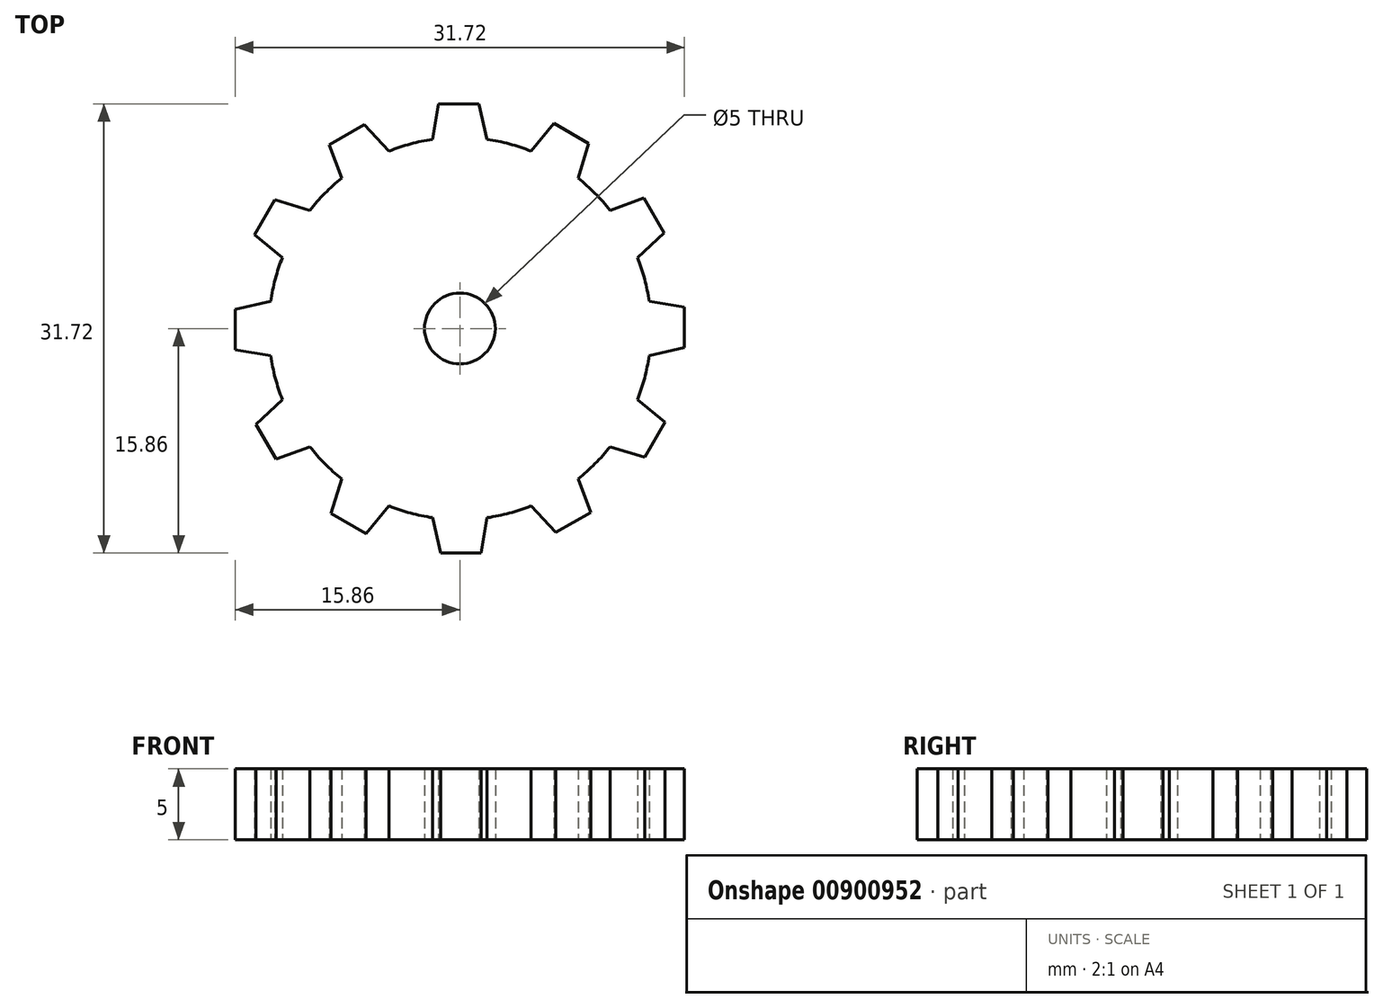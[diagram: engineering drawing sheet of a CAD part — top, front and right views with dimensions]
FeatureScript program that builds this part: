
annotation { "Feature Type Name" : "Feature", "Feature Type Description" : "" }
export const myFeature = defineFeature(function(context is Context, id is Id, definition is map)
    precondition{}
    {
        {
            var Q0;
            Q0=qCreatedBy(makeId("Top.planeOp"),FACE);
            var sketch = newSketch(context, id + "F0", { "sketchPlane" : qUnion([Q0])});
            skCircle(sketch, "E0", {"center": v(0, 0) * mm, "radius": 13.5 * mm});
            skLineSegment(sketch, "E1", {"start": v(-1.92, 13.36) * mm, "end": v(1.93, 13.36) * mm});
            skLineSegment(sketch, "E2", {"start": v(1.93, 13.36) * mm, "end": v(1.34, 15.86) * mm});
            skLineSegment(sketch, "E3", {"start": v(1.34, 15.86) * mm, "end": v(-1.5, 15.86) * mm});
            skLineSegment(sketch, "E4", {"start": v(-1.5, 15.86) * mm, "end": v(-1.92, 13.36) * mm});
            skLineSegment(sketch, "E5.1.0", {"start": v(-6.77, 14.4) * mm, "end": v(-9.23, 12.98) * mm});
            skLineSegment(sketch, "E5.1.1", {"start": v(-5.01, 12.53) * mm, "end": v(-6.77, 14.4) * mm});
            skLineSegment(sketch, "E5.1.2", {"start": v(-8.35, 10.6) * mm, "end": v(-5.01, 12.53) * mm});
            skLineSegment(sketch, "E5.1.3", {"start": v(-9.23, 12.98) * mm, "end": v(-8.35, 10.6) * mm});
            skLineSegment(sketch, "E5.2.0", {"start": v(-13.06, 9.1) * mm, "end": v(-14.49, 6.63) * mm});
            skLineSegment(sketch, "E5.2.1", {"start": v(-10.6, 8.35) * mm, "end": v(-13.06, 9.1) * mm});
            skLineSegment(sketch, "E5.2.2", {"start": v(-12.53, 5.01) * mm, "end": v(-10.6, 8.35) * mm});
            skLineSegment(sketch, "E5.2.3", {"start": v(-14.49, 6.63) * mm, "end": v(-12.53, 5.01) * mm});
            skLineSegment(sketch, "E6.2.3.0", {"start": v(-15.86, 1.34) * mm, "end": v(-15.86, -1.5) * mm});
            skLineSegment(sketch, "E6.3.3.0", {"start": v(-13.36, 1.93) * mm, "end": v(-15.86, 1.34) * mm});
            skLineSegment(sketch, "E6.6.3.0", {"start": v(-13.36, -1.93) * mm, "end": v(-13.36, 1.93) * mm});
            skLineSegment(sketch, "E6.9.3.0", {"start": v(-15.86, -1.5) * mm, "end": v(-13.36, -1.92) * mm});
            skLineSegment(sketch, "E6.2.4.0", {"start": v(-14.4, -6.77) * mm, "end": v(-12.98, -9.23) * mm});
            skLineSegment(sketch, "E6.3.4.0", {"start": v(-12.53, -5.01) * mm, "end": v(-14.4, -6.77) * mm});
            skLineSegment(sketch, "E6.6.4.0", {"start": v(-10.6, -8.35) * mm, "end": v(-12.53, -5.01) * mm});
            skLineSegment(sketch, "E6.9.4.0", {"start": v(-12.98, -9.23) * mm, "end": v(-10.6, -8.35) * mm});
            skLineSegment(sketch, "E6.2.5.0", {"start": v(-9.1, -13.06) * mm, "end": v(-6.63, -14.49) * mm});
            skLineSegment(sketch, "E6.3.5.0", {"start": v(-8.35, -10.6) * mm, "end": v(-9.1, -13.06) * mm});
            skLineSegment(sketch, "E6.6.5.0", {"start": v(-5.01, -12.53) * mm, "end": v(-8.35, -10.6) * mm});
            skLineSegment(sketch, "E6.9.5.0", {"start": v(-6.63, -14.49) * mm, "end": v(-5.01, -12.53) * mm});
            skLineSegment(sketch, "E6.2.6.0", {"start": v(-1.34, -15.86) * mm, "end": v(1.5, -15.86) * mm});
            skLineSegment(sketch, "E6.3.6.0", {"start": v(-1.93, -13.36) * mm, "end": v(-1.34, -15.86) * mm});
            skLineSegment(sketch, "E6.6.6.0", {"start": v(1.92, -13.36) * mm, "end": v(-1.93, -13.36) * mm});
            skLineSegment(sketch, "E6.9.6.0", {"start": v(1.5, -15.86) * mm, "end": v(1.92, -13.36) * mm});
            skLineSegment(sketch, "E6.2.7.0", {"start": v(6.77, -14.4) * mm, "end": v(9.23, -12.98) * mm});
            skLineSegment(sketch, "E6.3.7.0", {"start": v(5.01, -12.53) * mm, "end": v(6.77, -14.4) * mm});
            skLineSegment(sketch, "E6.6.7.0", {"start": v(8.35, -10.6) * mm, "end": v(5.01, -12.53) * mm});
            skLineSegment(sketch, "E6.9.7.0", {"start": v(9.23, -12.98) * mm, "end": v(8.35, -10.6) * mm});
            skLineSegment(sketch, "E6.2.8.0", {"start": v(13.06, -9.1) * mm, "end": v(14.49, -6.63) * mm});
            skLineSegment(sketch, "E6.3.8.0", {"start": v(10.6, -8.35) * mm, "end": v(13.06, -9.1) * mm});
            skLineSegment(sketch, "E6.6.8.0", {"start": v(12.53, -5.01) * mm, "end": v(10.6, -8.35) * mm});
            skLineSegment(sketch, "E6.9.8.0", {"start": v(14.49, -6.63) * mm, "end": v(12.53, -5.01) * mm});
            skLineSegment(sketch, "E6.2.9.0", {"start": v(15.86, -1.34) * mm, "end": v(15.86, 1.5) * mm});
            skLineSegment(sketch, "E6.3.9.0", {"start": v(13.36, -1.93) * mm, "end": v(15.86, -1.34) * mm});
            skLineSegment(sketch, "E6.6.9.0", {"start": v(13.36, 1.92) * mm, "end": v(13.36, -1.93) * mm});
            skLineSegment(sketch, "E6.9.9.0", {"start": v(15.86, 1.5) * mm, "end": v(13.36, 1.92) * mm});
            skLineSegment(sketch, "E6.2.10.0", {"start": v(14.4, 6.77) * mm, "end": v(12.98, 9.23) * mm});
            skLineSegment(sketch, "E6.3.10.0", {"start": v(12.53, 5.01) * mm, "end": v(14.4, 6.77) * mm});
            skLineSegment(sketch, "E6.6.10.0", {"start": v(10.6, 8.35) * mm, "end": v(12.53, 5.01) * mm});
            skLineSegment(sketch, "E6.9.10.0", {"start": v(12.98, 9.23) * mm, "end": v(10.6, 8.35) * mm});
            skLineSegment(sketch, "E6.2.11.0", {"start": v(9.1, 13.06) * mm, "end": v(6.63, 14.49) * mm});
            skLineSegment(sketch, "E6.3.11.0", {"start": v(8.35, 10.6) * mm, "end": v(9.1, 13.06) * mm});
            skLineSegment(sketch, "E6.6.11.0", {"start": v(5.01, 12.53) * mm, "end": v(8.35, 10.6) * mm});
            skLineSegment(sketch, "E6.9.11.0", {"start": v(6.63, 14.49) * mm, "end": v(5.01, 12.53) * mm});
            skCircle(sketch, "E7", {"center": v(0, 0) * mm, "radius": 2.5 * mm});
            skSolve(sketch);
        }
        {
            var Q0;
            Q0=makeQuery(id+"F0.imprint","IMPRINT",FACE,{"disambiguationData":[TD([[makeQuery(id+"F0.imprint","IMPRINT",EDGE,{"derivedFrom":sQuery(id+"F0.wireOp",EDGE,"E5.1.0")}),1.0]])]});
            var Q1;
            {var subQ8=sQuery(id+"F0.wireOp",EDGE,"E1");Q1=makeQuery(id+"F0.imprint","IMPRINT",FACE,{"disambiguationData":[TD([[makeQuery(id+"F0.imprint","IMPRINT",EDGE,{"derivedFrom":subQ8}),-1.0]])]});}
            var Q2;
            Q2=makeQuery(id+"F0.imprint","IMPRINT",FACE,{"disambiguationData":[TD([[makeQuery(id+"F0.imprint","IMPRINT",EDGE,{"derivedFrom":sQuery(id+"F0.wireOp",EDGE,"E5.2.0")}),1.0]])]});
            var Q3;
            {var subQ4=sQuery(id+"F0.wireOp",EDGE,"E6.2.3.0");Q3=makeQuery(id+"F0.imprint","IMPRINT",FACE,{"disambiguationData":[TD([[makeQuery(id+"F0.imprint","IMPRINT",EDGE,{"derivedFrom":subQ4}),1.0]])]});}
            var Q4;
            {var subQ5=sQuery(id+"F0.wireOp",EDGE,"E6.2.4.0");Q4=makeQuery(id+"F0.imprint","IMPRINT",FACE,{"disambiguationData":[TD([[makeQuery(id+"F0.imprint","IMPRINT",EDGE,{"derivedFrom":subQ5}),1.0]])]});}
            var Q5;
            {var subQ5=sQuery(id+"F0.wireOp",EDGE,"E6.2.5.0");Q5=makeQuery(id+"F0.imprint","IMPRINT",FACE,{"disambiguationData":[TD([[makeQuery(id+"F0.imprint","IMPRINT",EDGE,{"derivedFrom":subQ5}),1.0]])]});}
            var Q6;
            {var subQ5=sQuery(id+"F0.wireOp",EDGE,"E6.2.6.0");Q6=makeQuery(id+"F0.imprint","IMPRINT",FACE,{"disambiguationData":[TD([[makeQuery(id+"F0.imprint","IMPRINT",EDGE,{"derivedFrom":subQ5}),1.0]])]});}
            var Q7;
            {var subQ5=sQuery(id+"F0.wireOp",EDGE,"E6.2.7.0");Q7=makeQuery(id+"F0.imprint","IMPRINT",FACE,{"disambiguationData":[TD([[makeQuery(id+"F0.imprint","IMPRINT",EDGE,{"derivedFrom":subQ5}),1.0]])]});}
            var Q8;
            {var subQ5=sQuery(id+"F0.wireOp",EDGE,"E6.2.8.0");Q8=makeQuery(id+"F0.imprint","IMPRINT",FACE,{"disambiguationData":[TD([[makeQuery(id+"F0.imprint","IMPRINT",EDGE,{"derivedFrom":subQ5}),1.0]])]});}
            var Q9;
            {var subQ5=sQuery(id+"F0.wireOp",EDGE,"E6.2.9.0");Q9=makeQuery(id+"F0.imprint","IMPRINT",FACE,{"disambiguationData":[TD([[makeQuery(id+"F0.imprint","IMPRINT",EDGE,{"derivedFrom":subQ5}),1.0]])]});}
            var Q10;
            {var subQ5=sQuery(id+"F0.wireOp",EDGE,"E6.2.11.0");Q10=makeQuery(id+"F0.imprint","IMPRINT",FACE,{"disambiguationData":[TD([[makeQuery(id+"F0.imprint","IMPRINT",EDGE,{"derivedFrom":subQ5}),1.0]])]});}
            var Q11;
            {var subQ3=sQuery(id+"F0.wireOp",EDGE,"E2");Q11=makeQuery(id+"F0.imprint","IMPRINT",FACE,{"disambiguationData":[TD([[makeQuery(id+"F0.imprint","IMPRINT",EDGE,{"derivedFrom":subQ3}),1.0]])]});}
            var Q12;
            {var subQ5=sQuery(id+"F0.wireOp",EDGE,"E6.2.10.0");Q12=makeQuery(id+"F0.imprint","IMPRINT",FACE,{"disambiguationData":[TD([[makeQuery(id+"F0.imprint","IMPRINT",EDGE,{"derivedFrom":subQ5}),1.0]])]});}
            var Q13;
            {var subQ5=sQuery(id+"F0.wireOp",EDGE,"E6.6.9.0");Q13=makeQuery(id+"F0.imprint","IMPRINT",FACE,{"disambiguationData":[TD([[makeQuery(id+"F0.imprint","IMPRINT",EDGE,{"derivedFrom":subQ5}),1.0]])]});}
            var Q14;
            {var subQ5=sQuery(id+"F0.wireOp",EDGE,"E6.6.10.0");Q14=makeQuery(id+"F0.imprint","IMPRINT",FACE,{"disambiguationData":[TD([[makeQuery(id+"F0.imprint","IMPRINT",EDGE,{"derivedFrom":subQ5}),1.0]])]});}
            var Q15;
            {var subQ5=sQuery(id+"F0.wireOp",EDGE,"E6.6.11.0");Q15=makeQuery(id+"F0.imprint","IMPRINT",FACE,{"disambiguationData":[TD([[makeQuery(id+"F0.imprint","IMPRINT",EDGE,{"derivedFrom":subQ5}),1.0]])]});}
            var Q16;
            {var subQ0=sQuery(id+"F0.wireOp",EDGE,"E1");Q16=makeQuery(id+"F0.imprint","IMPRINT",FACE,{"disambiguationData":[TD([[makeQuery(id+"F0.imprint","IMPRINT",EDGE,{"derivedFrom":subQ0}),1.0]])]});}
            var Q17;
            {var subQ0=sQuery(id+"F0.wireOp",EDGE,"E5.1.2");var subQ1=sQuery(id+"F0.wireOp",EDGE,"E0");var subQ2=makeQuery(id+"F0.imprint","INTERSECT",VERTEX,{"disambiguationData":[OD(0.0)],"derivedFrom":[subQ1,subQ0]});Q17=makeQuery(id+"F0.imprint","IMPRINT",FACE,{"disambiguationData":[TD([[makeQuery(id+"F0.imprint","IMPRINT",EDGE,{"disambiguationData":[TD([[subQ2,-1.0]])],"derivedFrom":subQ1}),1.0]])]});}
            var Q18;
            {var subQ0=sQuery(id+"F0.wireOp",EDGE,"E5.2.2");var subQ1=sQuery(id+"F0.wireOp",EDGE,"E0");var subQ2=makeQuery(id+"F0.imprint","INTERSECT",VERTEX,{"disambiguationData":[OD(0.0)],"derivedFrom":[subQ1,subQ0]});Q18=makeQuery(id+"F0.imprint","IMPRINT",FACE,{"disambiguationData":[TD([[makeQuery(id+"F0.imprint","IMPRINT",EDGE,{"disambiguationData":[TD([[subQ2,-1.0]])],"derivedFrom":subQ1}),1.0]])]});}
            var Q19;
            {var subQ0=sQuery(id+"F0.wireOp",EDGE,"E6.6.3.0");var subQ1=sQuery(id+"F0.wireOp",EDGE,"E0");var subQ2=makeQuery(id+"F0.imprint","INTERSECT",VERTEX,{"derivedFrom":[subQ1,subQ0]});Q19=makeQuery(id+"F0.imprint","IMPRINT",FACE,{"disambiguationData":[TD([[makeQuery(id+"F0.imprint","IMPRINT",EDGE,{"disambiguationData":[TD([[subQ2,-1.0]])],"derivedFrom":subQ1}),1.0]])]});}
            var Q20;
            {var subQ5=sQuery(id+"F0.wireOp",EDGE,"E6.6.4.0");Q20=makeQuery(id+"F0.imprint","IMPRINT",FACE,{"disambiguationData":[TD([[makeQuery(id+"F0.imprint","IMPRINT",EDGE,{"derivedFrom":subQ5}),1.0]])]});}
            var Q21;
            {var subQ5=sQuery(id+"F0.wireOp",EDGE,"E6.6.5.0");Q21=makeQuery(id+"F0.imprint","IMPRINT",FACE,{"disambiguationData":[TD([[makeQuery(id+"F0.imprint","IMPRINT",EDGE,{"derivedFrom":subQ5}),1.0]])]});}
            var Q22;
            {var subQ5=sQuery(id+"F0.wireOp",EDGE,"E6.6.6.0");Q22=makeQuery(id+"F0.imprint","IMPRINT",FACE,{"disambiguationData":[TD([[makeQuery(id+"F0.imprint","IMPRINT",EDGE,{"derivedFrom":subQ5}),1.0]])]});}
            var Q23;
            {var subQ5=sQuery(id+"F0.wireOp",EDGE,"E6.6.7.0");Q23=makeQuery(id+"F0.imprint","IMPRINT",FACE,{"disambiguationData":[TD([[makeQuery(id+"F0.imprint","IMPRINT",EDGE,{"derivedFrom":subQ5}),1.0]])]});}
            var Q24;
            {var subQ5=sQuery(id+"F0.wireOp",EDGE,"E6.6.8.0");Q24=makeQuery(id+"F0.imprint","IMPRINT",FACE,{"disambiguationData":[TD([[makeQuery(id+"F0.imprint","IMPRINT",EDGE,{"derivedFrom":subQ5}),1.0]])]});}
            var Q25;
            {var subQ5=sQuery(id+"F0.wireOp",EDGE,"E6.6.3.0");Q25=makeQuery(id+"F0.imprint","IMPRINT",FACE,{"disambiguationData":[TD([[makeQuery(id+"F0.imprint","IMPRINT",EDGE,{"derivedFrom":subQ5}),1.0]])]});}
            var Q26;
            {var subQ5=sQuery(id+"F0.wireOp",EDGE,"E5.2.2");Q26=makeQuery(id+"F0.imprint","IMPRINT",FACE,{"disambiguationData":[TD([[makeQuery(id+"F0.imprint","IMPRINT",EDGE,{"derivedFrom":subQ5}),1.0]])]});}
            var Q27;
            {var subQ5=sQuery(id+"F0.wireOp",EDGE,"E5.1.2");Q27=makeQuery(id+"F0.imprint","IMPRINT",FACE,{"disambiguationData":[TD([[makeQuery(id+"F0.imprint","IMPRINT",EDGE,{"derivedFrom":subQ5}),1.0]])]});}
            extrude(context, id + "F1", {"entities" : qUnion([Q0, Q1, Q2, Q3, Q4, Q5, Q6, Q7, Q8, Q9, Q10, Q11, Q12, Q13, Q14, Q15, Q16, Q17, Q18, Q19, Q20, Q21, Q22, Q23, Q24, Q25, Q26, Q27]), "depth" : 5 * mm, "offsetDistance" : 25 * mm});
        }
    });
